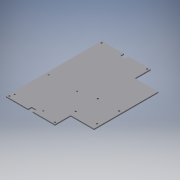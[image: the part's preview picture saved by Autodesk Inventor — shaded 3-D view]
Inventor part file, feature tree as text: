
AUTODESK INVENTOR PART (.ipt)
format: ipt  version: 2016 (Build 200138000, 138)  size: 190,976 bytes
history: native  units: in
note: dims shown in document units (in); Inventor stores cm internally (conversion verified against a paired STEP export)
features: extrude x5, sketch x5
ambient origin geometry x8: Origin, YZ Plane, XZ Plane, XY Plane, X Axis, Y Axis, Z Axis, Center Point
bodies: Body1 (feature_tree)
feature tree (10):
  extrude  "Extrusion2"  Depth=0.0394in
  extrude  "Extrusion3"  TaperAngle=0.0deg  [1 undecoded]
  extrude  "Extrusion4"  Depth=0.0787in TaperAngle=0.0deg
  extrude  "Extrusion5"  Depth=0.1181in
  extrude  "Extrusion6"  Depth=0.3937in
  sketch  "Sketch1"  dims[d0=0.0394in d4=0.0394in d5=0.0394in d6=0.0394in d7=0.0394in d8=0.0394in d10=0.0394in d11=0.0394in d12=0.0394in d13=0.0394in d14=0.0394in d15=0.0394in]
  sketch  "Sketch2"  dims[d16=0.2362in d17=0.0in]
  sketch  "Sketch3"  dims[d18=0.0in d21=0.0787in d22=0.0in]
  sketch  "Sketch4"  dims[d25=0.0394in d26=0.1181in]
  sketch  "Sketch5"  dims[d27=0.1181in d28=0.1181in d29=0.3937in d30=0.0in d31=1.9291in d32=2.2835in d33=1.9291in d34=2.2835in d35=0.3937in d36=0.3937in d37=0.1969in d38=0.1969in d39=0.3937in d40=0.0in d41=0.3937in d42=0.0in d43=0.7244in d44=1.4252in d45=0.7244in d46=1.4252in d47=1.4252in d48=1.4252in d49=0.3858in d50=0.3858in d51=0.1969in d52=0.1969in d53=1.4961in d54=1.4409in d55=1.4961in d56=1.4409in d57=1.4961in d58=1.4961in d59=0.1969in d60=0.3543in d61=0.3937in d62=0.0in]
note: 1 required parameter value undecoded (feature->parameter linkage not recoverable at this tier; creation-order binding heuristic only, values carry confidence <= 0.55)
